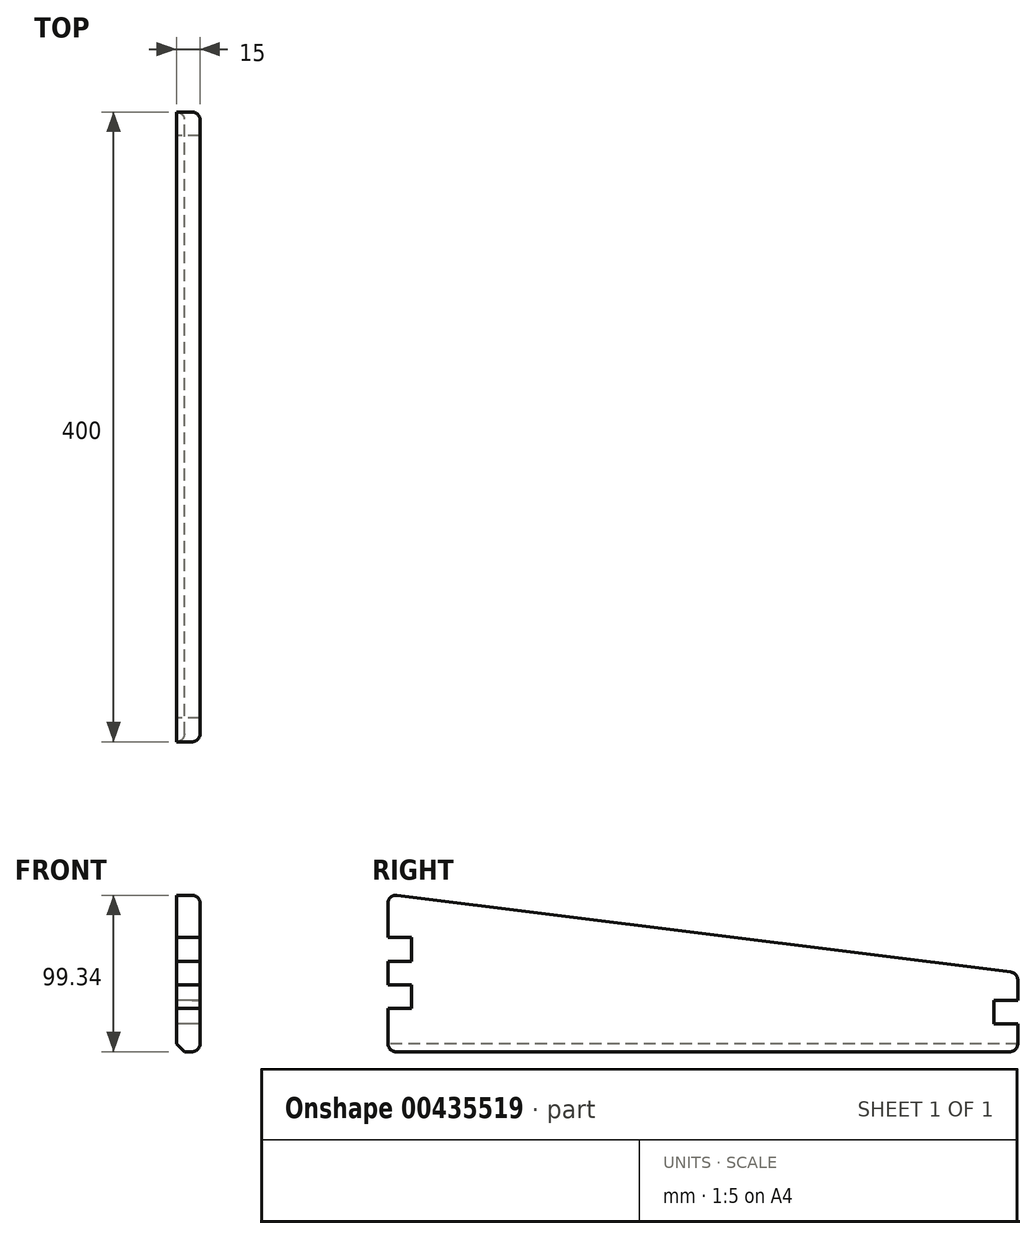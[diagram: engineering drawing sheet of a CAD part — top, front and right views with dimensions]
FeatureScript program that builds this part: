
annotation { "Feature Type Name" : "Feature", "Feature Type Description" : "" }
export const myFeature = defineFeature(function(context is Context, id is Id, definition is map)
    precondition{}
    {
        {
            var Q0;
            Q0=qCreatedBy(makeId("Right.planeOp"),FACE);
            var sketch = newSketch(context, id + "F0", { "sketchPlane" : qUnion([Q0])});
            skLineSegment(sketch, "E0.bottom", {"start": v(206.1, -35.37) * mm, "end": v(-193.9, -35.37) * mm});
            skPoint(sketch, "E0.middle", {"position": v(0, 0) * mm});
            skLineSegment(sketch, "E1", {"start": v(-193.9, 64.63) * mm, "end": v(206.1, 14.63) * mm});
            skLineSegment(sketch, "E2", {"start": v(-193.9, -7.87) * mm, "end": v(-178.9, -7.87) * mm});
            skLineSegment(sketch, "E3", {"start": v(-178.9, -7.87) * mm, "end": v(-178.9, 7.13) * mm});
            skLineSegment(sketch, "E4", {"start": v(-178.9, 7.13) * mm, "end": v(-193.9, 7.13) * mm});
            skLineSegment(sketch, "E5", {"start": v(-193.9, -7.87) * mm, "end": v(-193.9, -35.37) * mm});
            skLineSegment(sketch, "E6", {"start": v(-193.9, 7.13) * mm, "end": v(-193.9, 22.13) * mm});
            skLineSegment(sketch, "E7", {"start": v(-193.9, 22.13) * mm, "end": v(-178.9, 22.13) * mm});
            skLineSegment(sketch, "E8", {"start": v(-178.9, 22.13) * mm, "end": v(-178.9, 37.13) * mm});
            skLineSegment(sketch, "E9", {"start": v(-178.9, 37.13) * mm, "end": v(-193.9, 37.13) * mm});
            skLineSegment(sketch, "E10", {"start": v(-193.9, 64.63) * mm, "end": v(-193.9, 37.13) * mm});
            skLineSegment(sketch, "E11", {"start": v(206.1, -2.87) * mm, "end": v(191.1, -2.87) * mm});
            skLineSegment(sketch, "E12", {"start": v(191.1, -2.87) * mm, "end": v(191.1, -17.87) * mm});
            skLineSegment(sketch, "E13", {"start": v(191.1, -17.87) * mm, "end": v(206.1, -17.87) * mm});
            skLineSegment(sketch, "E14", {"start": v(206.1, 14.63) * mm, "end": v(206.1, -2.87) * mm});
            skLineSegment(sketch, "E15", {"start": v(206.1, -17.87) * mm, "end": v(206.1, -35.37) * mm});
            skSolve(sketch);
        }
        {
            var Q0;
            Q0=makeQuery(id+"F0.imprint","IMPRINT",FACE,{"disambiguationData":[TD([[makeQuery(id+"F0.imprint","IMPRINT",EDGE,{"derivedFrom":sQuery(id+"F0.wireOp",EDGE,"E0.bottom")}),-1.0]])]});
            extrude(context, id + "F1", {"entities" : qUnion([Q0]), "depth" : 15 * mm});
        }
        {
            var Q0;
            Q0=makeQuery(id+"F1.opExtrude","CAP_EDGE",EDGE,{"disambiguationData":[OSD([sQuery(id+"F0.wireOp",EDGE,"E14")])],"isStart":false});
            var Q1;
            Q1=makeQuery(id+"F1.opExtrude","CAP_EDGE",EDGE,{"disambiguationData":[OSD([sQuery(id+"F0.wireOp",EDGE,"E15")])],"isStart":false});
            var Q2;
            Q2=makeQuery(id+"F1.opExtrude","CAP_EDGE",EDGE,{"disambiguationData":[OSD([sQuery(id+"F0.wireOp",EDGE,"E5")])],"isStart":false});
            var Q3;
            Q3=makeQuery(id+"F1.opExtrude","CAP_EDGE",EDGE,{"disambiguationData":[OSD([sQuery(id+"F0.wireOp",EDGE,"E6")])],"isStart":false});
            var Q4;
            Q4=makeQuery(id+"F1.opExtrude","CAP_EDGE",EDGE,{"disambiguationData":[OSD([sQuery(id+"F0.wireOp",EDGE,"E10")])],"isStart":false});
            fillet(context, id + "F2", {"entities" : qUnion([Q0, Q1, Q2, Q3, Q4]), "radius" : 5 * mm, "tangentPropagation" : true, "allowEdgeOverflow" : false});
        }
        {
            var Q0;
            Q0=makeQuery(id+"F1.opExtrude","CAP_EDGE",EDGE,{"disambiguationData":[OSD([sQuery(id+"F0.wireOp",EDGE,"E1")])],"isStart":false});
            fillet(context, id + "F3", {"entities" : qUnion([Q0]), "radius" : 5 * mm, "tangentPropagation" : true, "allowEdgeOverflow" : false});
        }
        {
            var Q0;
            Q0=makeQuery(id+"F1.opExtrude","CAP_EDGE",EDGE,{"disambiguationData":[OSD([sQuery(id+"F0.wireOp",EDGE,"E0.bottom")])],"isStart":false});
            fillet(context, id + "F4", {"entities" : qUnion([Q0]), "radius" : 5 * mm, "tangentPropagation" : true, "allowEdgeOverflow" : false});
        }
        {
            var Q0;
            Q0=makeQuery(id+"F1.opExtrude","CAP_EDGE",EDGE,{"disambiguationData":[OSD([sQuery(id+"F0.wireOp",EDGE,"E0.bottom")])],"isStart":true});
            chamfer(context, id + "F5", {"entities" : qUnion([Q0]), "width" : 5 * mm});
        }
    });
